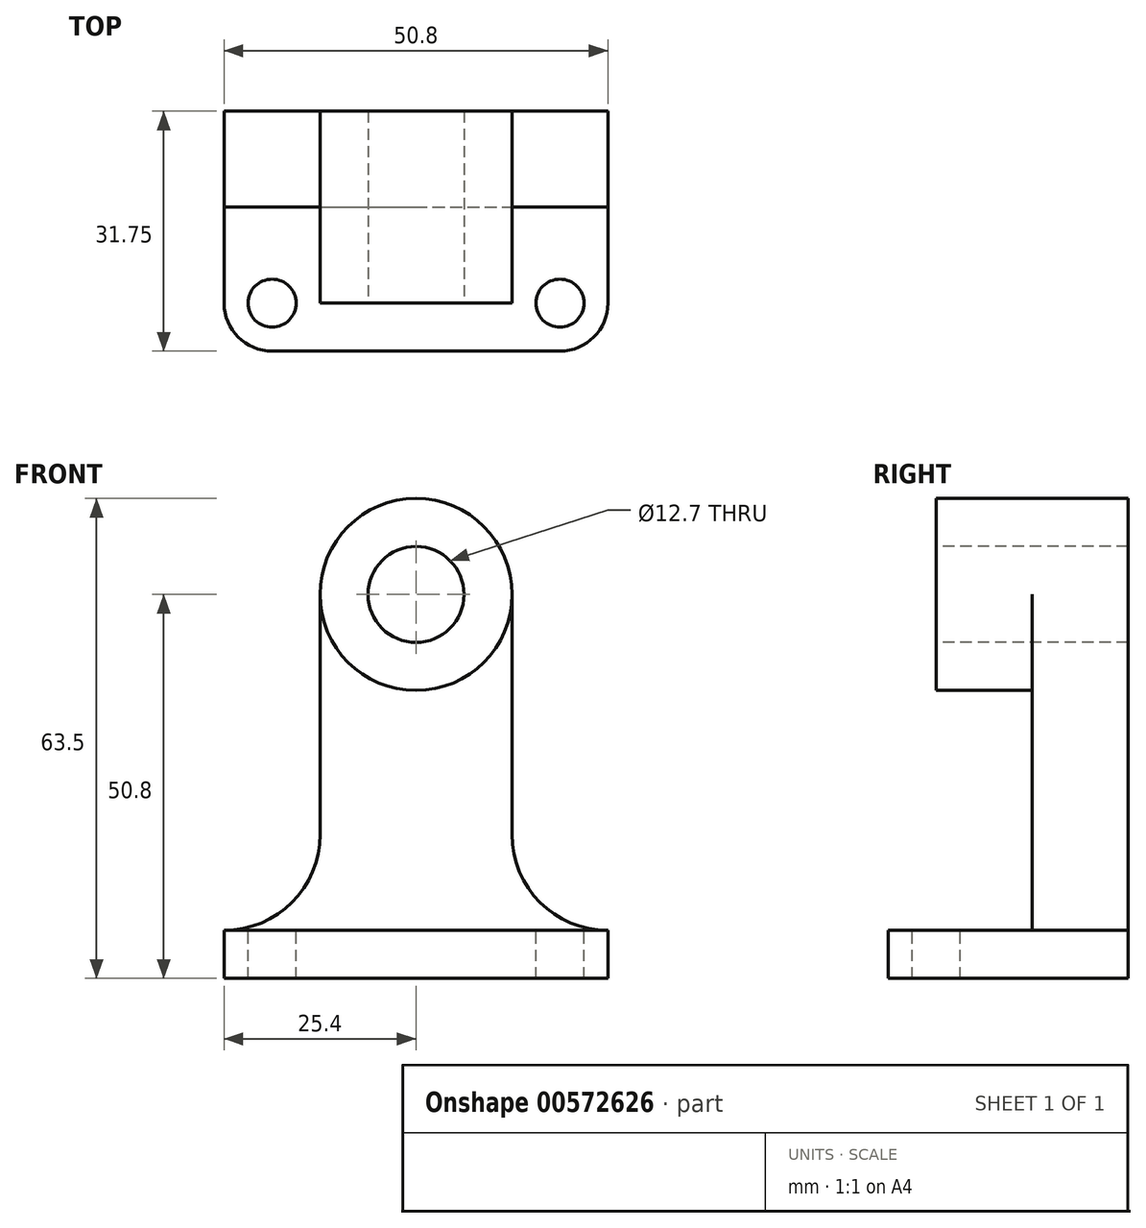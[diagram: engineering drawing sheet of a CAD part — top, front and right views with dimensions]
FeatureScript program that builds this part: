
annotation { "Feature Type Name" : "Feature", "Feature Type Description" : "" }
export const myFeature = defineFeature(function(context is Context, id is Id, definition is map)
    precondition{}
    {
        {
            var Q0;
            Q0=qCreatedBy(makeId("Front.planeOp"),FACE);
            var sketch = newSketch(context, id + "F0", { "sketchPlane" : qUnion([Q0])});
            skLineSegment(sketch, "E0", {"start": v(0, 0) * mm, "end": v(50.8, 0) * mm});
            skLineSegment(sketch, "E1", {"start": v(50.8, 0) * mm, "end": v(50.8, 63.5) * mm});
            skLineSegment(sketch, "E2", {"start": v(50.8, 63.5) * mm, "end": v(0, 63.5) * mm});
            skLineSegment(sketch, "E3", {"start": v(0, 63.5) * mm, "end": v(0, 0) * mm});
            skSolve(sketch);
        }
        {
            var Q0;
            Q0 = qSketchRegion(id + "F0", true);
            extrude(context, id + "F1", {"entities" : qUnion([Q0]), "depth" : 31.75 * mm, "offsetDistance" : 25.4 * mm});
        }
        {
            var Q0;
            Q0=makeQuery(id+"F1.opExtrude","SWEPT_FACE",FACE,{"disambiguationData":[OSD([sQuery(id+"F0.wireOp",EDGE,"E1")])]});
            var sketch = newSketch(context, id + "F2", { "sketchPlane" : qUnion([Q0])});
            skLineSegment(sketch, "E4", {"start": v(-31.75, 0) * mm, "end": v(-31.75, 6.35) * mm});
            skLineSegment(sketch, "E5", {"start": v(-31.75, 6.35) * mm, "end": v(-12.7, 6.35) * mm});
            skLineSegment(sketch, "E6", {"start": v(-12.7, 6.35) * mm, "end": v(-12.7, 38.1) * mm});
            skLineSegment(sketch, "E7", {"start": v(-12.7, 38.1) * mm, "end": v(-25.4, 38.1) * mm});
            skLineSegment(sketch, "E8", {"start": v(-25.4, 38.1) * mm, "end": v(-25.4, 63.5) * mm});
            skSolve(sketch);
        }
        {
            var Q0;
            Q0 = qSketchRegion(id + "F2", true);
            var Q1;
            {var subQ1=sQuery(id+"F2.wireOp",EDGE,"E5");Q1=makeQuery(id+"F2.imprint","IMPRINT",FACE,{"disambiguationData":[TD([[makeQuery(id+"F2.imprint","IMPRINT",EDGE,{"derivedFrom":subQ1}),1.0]])]});}
            extrude(context, id + "F3", {"entities" : qUnion([Q0, Q1]), "operationType" : NewBodyOperationType.REMOVE, "oppositeDirection" : true, "depth" : 50.8 * mm, "offsetDistance" : 25.4 * mm});
        }
        {
            var Q0;
            Q0=makeQuery(id+"F3.boolean.opBoolean","COPY",FACE,{"derivedFrom":makeQuery(id+"F3.opExtrude","SWEPT_FACE",FACE,{"disambiguationData":[OSD([sQuery(id+"F2.wireOp",EDGE,"E6")])]})});
            var sketch = newSketch(context, id + "F4", { "sketchPlane" : qUnion([Q0])});
            skLineSegment(sketch, "E9", {"start": v(50.8, 38.1) * mm, "end": v(38.1, 38.1) * mm});
            skLineSegment(sketch, "E10", {"start": v(38.1, 38.1) * mm, "end": v(38.1, 19.05) * mm});
            skLineSegment(sketch, "E11", {"start": v(38.1, 19.05) * mm, "end": v(38.1, 6.35) * mm});
            skArc(sketch, "E12", {"start": v(38.1, 19.05) * mm, "mid": v(41.82, 10.07) * mm, "end": v(50.8, 6.35) * mm});
            skLineSegment(sketch, "E13", {"start": v(12.7, 19.05) * mm, "end": v(12.7, 38.1) * mm});
            skLineSegment(sketch, "E14", {"start": v(12.7, 38.1) * mm, "end": v(0, 38.1) * mm});
            skArc(sketch, "E15", {"start": v(0, 6.35) * mm, "mid": v(8.98, 10.07) * mm, "end": v(12.7, 19.05) * mm});
            skSolve(sketch);
        }
        {
            var Q0;
            Q0 = qSketchRegion(id + "F4", true);
            var Q1;
            Q1=makeQuery(id+"F4.imprint","IMPRINT",FACE,{"disambiguationData":[TD([[makeQuery(id+"F4.imprint","IMPRINT",EDGE,{"derivedFrom":sQuery(id+"F4.wireOp",EDGE,"E13")}),1.0]])]});
            var Q2;
            Q2=makeQuery(id+"F4.imprint","IMPRINT",FACE,{"disambiguationData":[TD([[makeQuery(id+"F4.imprint","IMPRINT",EDGE,{"derivedFrom":sQuery(id+"F4.wireOp",EDGE,"E9")}),-1.0]])]});
            extrude(context, id + "F5", {"entities" : qUnion([Q0, Q1, Q2]), "operationType" : NewBodyOperationType.REMOVE, "oppositeDirection" : true, "depth" : 12.7 * mm, "offsetDistance" : 25.4 * mm});
        }
        {
            var Q0;
            Q0=makeQuery(id+"F3.boolean.opBoolean","COPY",FACE,{"derivedFrom":makeQuery(id+"F3.opExtrude","SWEPT_FACE",FACE,{"disambiguationData":[OSD([sQuery(id+"F2.wireOp",EDGE,"E8")])]})});
            var sketch = newSketch(context, id + "F6", { "sketchPlane" : qUnion([Q0])});
            skLineSegment(sketch, "E16", {"start": v(0, 38.1) * mm, "end": v(12.7, 38.1) * mm});
            skLineSegment(sketch, "E17", {"start": v(12.7, 38.1) * mm, "end": v(12.7, 63.5) * mm});
            skLineSegment(sketch, "E18", {"start": v(50.8, 38.1) * mm, "end": v(38.1, 38.1) * mm});
            skLineSegment(sketch, "E19", {"start": v(38.1, 38.1) * mm, "end": v(38.1, 63.5) * mm});
            skCircle(sketch, "E20", {"center": v(25.4, 50.8) * mm, "radius": 12.7 * mm});
            skPoint(sketch, "E20.centerSnap0", {"position": v(12.7, 50.8) * mm});
            skPoint(sketch, "E20.centerSnap1", {"position": v(25.4, 38.1) * mm});
            skCircle(sketch, "E21", {"center": v(25.4, 50.8) * mm, "radius": 6.35 * mm});
            skSolve(sketch);
        }
        {
            var Q0;
            {var subQ0=sQuery(id+"F6.wireOp",EDGE,"E19");var subQ3=sQuery(id+"F6.wireOp",EDGE,"E20");var subQ4=makeQuery(id+"F6.imprint","INTERSECT",VERTEX,{"derivedFrom":[subQ0,subQ3]});Q0=makeQuery(id+"F6.imprint","IMPRINT",FACE,{"disambiguationData":[TD([[makeQuery(id+"F6.imprint","IMPRINT",EDGE,{"disambiguationData":[TD([[subQ4,1.0]])],"derivedFrom":subQ3}),-1.0]])]});}
            var Q1;
            {var subQ0=sQuery(id+"F6.wireOp",EDGE,"E17");var subQ3=sQuery(id+"F6.wireOp",EDGE,"E20");var subQ4=makeQuery(id+"F6.imprint","INTERSECT",VERTEX,{"derivedFrom":[subQ0,subQ3]});Q1=makeQuery(id+"F6.imprint","IMPRINT",FACE,{"disambiguationData":[TD([[makeQuery(id+"F6.imprint","IMPRINT",EDGE,{"disambiguationData":[TD([[subQ4,-1.0]])],"derivedFrom":subQ3}),-1.0]])]});}
            extrude(context, id + "F7", {"entities" : qUnion([Q0, Q1]), "operationType" : NewBodyOperationType.REMOVE, "oppositeDirection" : true, "depth" : 12.7 * mm, "offsetDistance" : 25.4 * mm});
        }
        {
            var Q0;
            Q0=makeQuery(id+"F6.imprint","IMPRINT",FACE,{"disambiguationData":[TD([[makeQuery(id+"F6.imprint","IMPRINT",EDGE,{"derivedFrom":sQuery(id+"F6.wireOp",EDGE,"E21")}),1.0]])]});
            var Q1;
            {var subQ3=sQuery(id+"F6.wireOp",EDGE,"E16");Q1=makeQuery(id+"F6.imprint","IMPRINT",FACE,{"disambiguationData":[TD([[makeQuery(id+"F6.imprint","IMPRINT",EDGE,{"derivedFrom":subQ3}),1.0]])]});}
            var Q2;
            {var subQ6=sQuery(id+"F6.wireOp",EDGE,"E18");Q2=makeQuery(id+"F6.imprint","IMPRINT",FACE,{"disambiguationData":[TD([[makeQuery(id+"F6.imprint","IMPRINT",EDGE,{"derivedFrom":subQ6}),1.0]])]});}
            var Q3;
            {var subQ0=sQuery(id+"F6.wireOp",EDGE,"E19");var subQ3=sQuery(id+"F6.wireOp",EDGE,"E20");var subQ4=makeQuery(id+"F6.imprint","INTERSECT",VERTEX,{"derivedFrom":[subQ0,subQ3]});Q3=makeQuery(id+"F6.imprint","IMPRINT",FACE,{"disambiguationData":[TD([[makeQuery(id+"F6.imprint","IMPRINT",EDGE,{"disambiguationData":[TD([[subQ4,-1.0]])],"derivedFrom":subQ0}),1.0]])]});}
            var Q4;
            {var subQ0=sQuery(id+"F6.wireOp",EDGE,"E17");var subQ3=sQuery(id+"F6.wireOp",EDGE,"E20");var subQ4=makeQuery(id+"F6.imprint","INTERSECT",VERTEX,{"derivedFrom":[subQ0,subQ3]});Q4=makeQuery(id+"F6.imprint","IMPRINT",FACE,{"disambiguationData":[TD([[makeQuery(id+"F6.imprint","IMPRINT",EDGE,{"disambiguationData":[TD([[subQ4,-1.0]])],"derivedFrom":subQ0}),-1.0]])]});}
            extrude(context, id + "F8", {"entities" : qUnion([Q0, Q1, Q2, Q3, Q4]), "operationType" : NewBodyOperationType.REMOVE, "oppositeDirection" : true, "depth" : 25.4 * mm, "offsetDistance" : 25.4 * mm});
        }
        {
            var Q0;
            Q0=makeQuery(id+"F3.boolean.opBoolean","COPY",FACE,{"derivedFrom":makeQuery(id+"F3.opExtrude","SWEPT_FACE",FACE,{"disambiguationData":[OSD([sQuery(id+"F2.wireOp",EDGE,"E5")])]})});
            var sketch = newSketch(context, id + "F9", { "sketchPlane" : qUnion([Q0])});
            skArc(sketch, "E22", {"start": v(0, -25.4) * mm, "mid": v(1.86, -29.9) * mm, "end": v(6.35, -31.75) * mm});
            skArc(sketch, "E23", {"start": v(44.45, -31.75) * mm, "mid": v(48.94, -29.9) * mm, "end": v(50.8, -25.4) * mm});
            skCircle(sketch, "E24", {"center": v(6.35, -25.4) * mm, "radius": 3.18 * mm});
            skCircle(sketch, "E25", {"center": v(44.45, -25.4) * mm, "radius": 3.18 * mm});
            skSolve(sketch);
        }
        {
            var Q0;
            Q0 = qSketchRegion(id + "F9", true);
            var Q1;
            {var subQ0=sQuery(id+"F9.wireOp",EDGE,"E22");Q1=makeQuery(id+"F9.imprint","IMPRINT",FACE,{"disambiguationData":[TD([[makeQuery(id+"F9.imprint","IMPRINT",EDGE,{"derivedFrom":subQ0}),-1.0]])]});}
            var Q2;
            {var subQ0=sQuery(id+"F9.wireOp",EDGE,"E23");Q2=makeQuery(id+"F9.imprint","IMPRINT",FACE,{"disambiguationData":[TD([[makeQuery(id+"F9.imprint","IMPRINT",EDGE,{"derivedFrom":subQ0}),-1.0]])]});}
            extrude(context, id + "F10", {"entities" : qUnion([Q0, Q1, Q2]), "operationType" : NewBodyOperationType.REMOVE, "oppositeDirection" : true, "depth" : 6.35 * mm, "offsetDistance" : 25.4 * mm});
        }
    });
